annotation { "Feature Type Name" : "Feature", "Feature Type Description" : "" }
export const myFeature = defineFeature(function(context is Context, id is Id, definition is map)
    precondition{}
    {
        {
            var Q0;
            Q0=qCreatedBy(makeId("Front.planeOp"),FACE);
            var sketch = newSketch(context, id + "F0", { "sketchPlane" : qUnion([Q0])});
            skLineSegment(sketch, "E0.bottom", {"start": v(23.5, -10) * mm, "end": v(-23.5, -10) * mm});
            skLineSegment(sketch, "E0.top", {"start": v(23.5, 10) * mm, "end": v(-23.5, 10) * mm});
            skLineSegment(sketch, "E0.left", {"start": v(23.5, -10) * mm, "end": v(23.5, 10) * mm});
            skLineSegment(sketch, "E0.right", {"start": v(-23.5, -10) * mm, "end": v(-23.5, 10) * mm});
            skPoint(sketch, "E0.middle", {"position": v(0, 0) * mm});
            skLineSegment(sketch, "E1.0", {"start": v(25.5, 12) * mm, "end": v(-25.5, 12) * mm});
            skLineSegment(sketch, "E1.1", {"start": v(25.5, -12) * mm, "end": v(25.5, 12) * mm});
            skLineSegment(sketch, "E1.2", {"start": v(25.5, -12) * mm, "end": v(-25.5, -12) * mm});
            skLineSegment(sketch, "E1.3", {"start": v(-25.5, -12) * mm, "end": v(-25.5, 12) * mm});
            skSolve(sketch);
        }
        {
            var Q0;
            Q0=makeQuery(id+"F0.imprint","IMPRINT",FACE,{"disambiguationData":[TD([[makeQuery(id+"F0.imprint","IMPRINT",EDGE,{"derivedFrom":sQuery(id+"F0.wireOp",EDGE,"E0.bottom")}),1.0]])]});
            extrude(context, id + "F1", {"entities" : qUnion([Q0]), "depth" : 60 * mm});
        }
        {
            var Q0;
            Q0=makeQuery(id+"F1.opExtrude","SWEPT_EDGE",EDGE,{"disambiguationData":[OSD([sQuery(id+"F0.wireOp",EDGE,"E1.0"),sQuery(id+"F0.wireOp",EDGE,"E1.3")])]});
            var Q1;
            Q1=makeQuery(id+"F1.opExtrude","SWEPT_EDGE",EDGE,{"disambiguationData":[OSD([sQuery(id+"F0.wireOp",EDGE,"E1.0"),sQuery(id+"F0.wireOp",EDGE,"E1.1")])]});
            fillet(context, id + "F2", {"entities" : qUnion([Q0, Q1]), "radius" : 3 * mm, "tangentPropagation" : true, "allowEdgeOverflow" : false});
        }
        {
            var Q0;
            Q0=makeQuery(id+"F1.opExtrude","CAP_FACE",FACE,{"disambiguationData":[OSD([sQuery(id+"F0.wireOp",EDGE,"E0.bottom"),sQuery(id+"F0.wireOp",EDGE,"E0.top"),sQuery(id+"F0.wireOp",EDGE,"E0.left"),sQuery(id+"F0.wireOp",EDGE,"E0.right"),sQuery(id+"F0.wireOp",EDGE,"E1.0"),sQuery(id+"F0.wireOp",EDGE,"E1.1"),sQuery(id+"F0.wireOp",EDGE,"E1.2"),sQuery(id+"F0.wireOp",EDGE,"E1.3")])],"isStart":false});
            var sketch = newSketch(context, id + "F3", { "sketchPlane" : qUnion([Q0])});
            skLineSegment(sketch, "E2.0", {"start": v(23.5, 10) * mm, "end": v(-23.5, 10) * mm});
            skLineSegment(sketch, "E3.0", {"start": v(-23.5, -10) * mm, "end": v(-23.5, 10) * mm});
            skLineSegment(sketch, "E4.0", {"start": v(23.5, -10) * mm, "end": v(-23.5, -10) * mm});
            skLineSegment(sketch, "E5.0", {"start": v(23.5, -10) * mm, "end": v(23.5, 10) * mm});
            skLineSegment(sketch, "E6", {"start": v(-23.5, 10) * mm, "end": v(-23.5, -10) * mm});
            skSolve(sketch);
        }
        {
            var Q0;
            Q0=makeQuery(id+"F3.imprint","IMPRINT",FACE,{"disambiguationData":[TD([[makeQuery(id+"F3.imprint","IMPRINT",EDGE,{"derivedFrom":sQuery(id+"F3.wireOp",EDGE,"E2.0")}),1.0]])]});
            extrude(context, id + "F4", {"entities" : qUnion([Q0]), "operationType" : NewBodyOperationType.ADD, "oppositeDirection" : true, "depth" : 1 * mm});
        }
        {
            var Q0;
            Q0=makeQuery(id+"F1.opExtrude","SWEPT_FACE",FACE,{"disambiguationData":[OSD([sQuery(id+"F0.wireOp",EDGE,"E1.0")])]});
            var sketch = newSketch(context, id + "F5", { "sketchPlane" : qUnion([Q0])});
            skText(sketch, "E7", { "text": "Hex Wrenches\n", "fontName": "OpenSans-Regular.ttf"});
            skText(sketch, "E8", { "text": "Metric", "fontName": "OpenSans-Bold.ttf"});
            const initialGuessF5  = {"E7": [-0.0202, -0.01928, 1, 0, 0.00427], "E8": [-0.01582, -0.03033, 1, 0, 0.0068]};
            skSetInitialGuess(sketch, initialGuessF5);
            skSolve(sketch);
        }
        {
            var Q0;
            Q0 = qSketchRegion(id + "F5", true);
            extrude(context, id + "F6", {"entities" : qUnion([Q0]), "operationType" : NewBodyOperationType.REMOVE, "endBound" : BoundingType.SYMMETRIC, "oppositeDirection" : true, "depth" : 0.5 * mm});
        }
    });